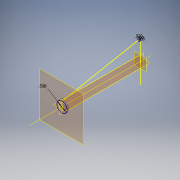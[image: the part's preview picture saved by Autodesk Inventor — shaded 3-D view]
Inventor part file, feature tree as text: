
AUTODESK INVENTOR PART (.ipt)
format: ipt  version: 2018 (Build 220112000, 112)  size: 332,288 bytes
history: native  units: in
note: dims shown in document units (in); Inventor stores cm internally (conversion verified against a paired STEP export)
features: sketch x5, other x2, helix x2, plane x1, loft x1, hole x1, extrude x1, projected_geometry x1
ambient origin geometry x8: Origin, YZ Plane, XZ Plane, XY Plane, X Axis, Y Axis, Z Axis, Center Point
bodies: Solid1 (feature_tree)
feature tree (14):
  sketch  "Sketch1"  dims[d0=2.0in d2=3.9in]
  plane  "Work Plane1"
  loft  "Loft1"
  other  "Work Point1"
  hole  "Hole1"  [1 undecoded]
  other  "Work Axis2"
  sketch  "Sketch6"  dims[d65=1.0in d66=1.0in d11=0.178in d12=0.75in d13=0.375in d14=0.25in d15=0.5635in d16=1.0in d17=0.8108in d41=0.1in]
  helix  "Coil3"  [1 undecoded]
  helix  "Coil4"  [1 undecoded]
  extrude  "Extrusion2"  Depth=0.02in
  sketch  "Sketch9"  dims[d44=0.13in d45=1.0in d46=11.811in d47=-0.0739in d48=90.0deg d49=90.0deg d50=0.0in d51=0.0in d52=0.13in d53=1.0in d54=11.811in d55=0.0756in d56=90.0deg d57=90.0deg d58=0.0in d59=0.0in d60=3.775in d61=3.0in d62=0.0in]
  sketch  "Sketch2"  dims[d3=0.5in d5=0.0in d6=90.0deg d7=0.0in d8=90.0deg]
  projected_geometry  "Projected Loop1"
  sketch  "Sketch8"  dims[d42=0.1in d43=0.02in]
note: 3 required parameter values undecoded (feature->parameter linkage not recoverable at this tier; creation-order binding heuristic only, values carry confidence <= 0.55)
